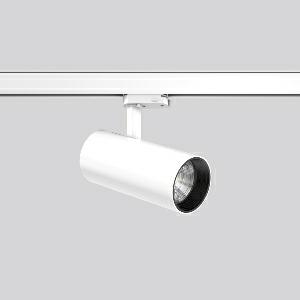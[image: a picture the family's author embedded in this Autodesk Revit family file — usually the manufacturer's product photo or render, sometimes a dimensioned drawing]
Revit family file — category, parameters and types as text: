
# Revit family: deecos_s_mini_742206_002_1_f26f
name_source: partatom
category: Lighting Fixtures
units: mm (PartAtom-declared; Revit-internal decimal feet)

## family parameters
Cut with Voids When Loaded = No
Host = Face
Light Source = No
Part Type = Normal
Room Calculation Point = No
Round Connector Dimension = Use Diameter
Shared = No

## types (1)
- DEECOS S mini (1 x LED Modul 940, 3400 lm, 4000)
    Apparent Load = 29 VA
    Approval mark = CE
    CIE Flux Codes = 99 100 100 100 100
    Color Rendering = 92
    Color Temperature = 4000
    Default Elevation = 1800 mm
    Description = Series: DEECOS S mini
LED surface-mounted projector in modern design with no visible cooling ribs. Housing: die-cast aluminium, powder-coated. Rotation range: 356°. Swivel range: 90°. Black plastic ring and recessed LED to prevent glare from the side. Optical assembly with lens made of plastic (polycarbonate) for the best homogeneous light distribution - can be changed without tools. Best colour rendering index Ra>90. With multi adaptor for 3-circuit tracks 230 V. Suitable for Track on ceiling, Wall track. High quality converter without flickering and stroboscopic effect. The following accessories can be mounted without use of tools: interchangeable lenses, decorative glasses, honeycomb louvre, clear and frosted diffusers, white interchangeable plastic ring. 
Colour: traffic white, matt (RAL 9016)
Diameter: 87 mm
Height: 214 mm
Lamp: LED
Socket: without socket
Colour temperature: 4000K
Colour rendering index (CRI): 92
System power: 29 W
Rated luminous flux: 3400 lm
Luminous efficiency: 117 lm/W
Control gear: Regulated power supply
Protection class: I
Type of protection: IP 20
    Height = 214 mm
    Lamp = 1 x LED Modul 940
    Lamp Light Flux = 3400 lm
    Lamp count = 1
    Length = 87 mm
    Lifetime = 50000 h
    Luminous efficacy = 117 lm/W
    Manufacturer = RZB
    ModVariant = No
    Model = 742206.002.1
    Mounting Place = Ceiling
    Mounting Type = Rail mounted
    Number of Poles = 1
    OnlyDefault = Yes
    Power Factor = 1
    Product Name = DEECOS S mini
    Product group = Track mounted projectors
    ProductGroupID = 301
    Protection Class = Protection class I
    Protection Degree = IP 20
    RLX_Detail_Level = 1
    RLX_Emergency_Light_Flux = 0 lm
    RLX_Emergency_Type = 0
    RLX_Emergency_Type_DB = No
    RlxData = <blob elided: 35885 chars, md5=b66e383d>
    Socket = socket
    Standby Power = 0 W
    System Light Flux = 3400 lm
    System Power = 29 W
    Type Comments = Product without accessories
    Type Image = 741930.002.jpg
    URL = http://relux.com
    VarID = ---
    Voltage = 230 V
    Voltage Range = 220-240 V
    Weight = 0.00 kg
    Width = 0 mm  [stored 0 ft]

note: [stored X ft] marks values corroborated as IEEE doubles in the binary element streams (Revit-internal decimal feet)

## geometry (parser evidence)
native form markers: Blend x4, Sweep x12
no freeform markers — native parametric forms only
